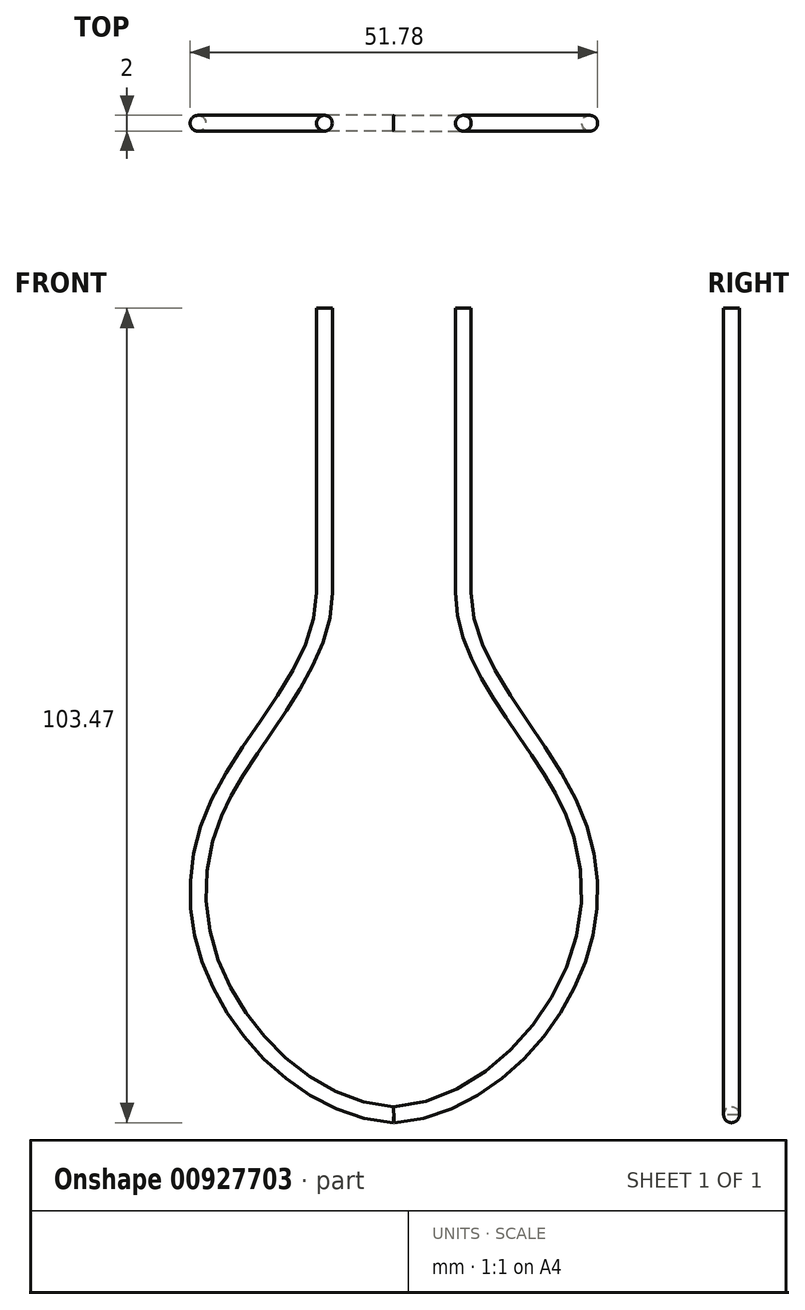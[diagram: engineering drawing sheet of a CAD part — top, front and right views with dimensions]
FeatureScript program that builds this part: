
annotation { "Feature Type Name" : "Feature", "Feature Type Description" : "" }
export const myFeature = defineFeature(function(context is Context, id is Id, definition is map)
    precondition{}
    {
        {
            var Q0;
            Q0=qCreatedBy(makeId("Top.planeOp"),FACE);
            cPlane(context, id + "F0", {"entities" : qUnion([Q0]), "cplaneType" : CPlaneType.OFFSET, "offset" : 83.57 * mm, "width" : 152.4 * mm, "height" : 152.4 * mm});
        }
        {
            var Q0;
            Q0=qCreatedBy(makeId("Front.planeOp"),FACE);
            var sketch = newSketch(context, id + "F1", { "sketchPlane" : qUnion([Q0])});
            skLineSegment(sketch, "E0", {"start": v(8.85, 83.91) * mm, "end": v(8.85, 47.77) * mm});
            skFitSpline(sketch, "E1", {"points": [v(8.85, 47.77) * mm, v(22.55, 20.49) * mm, v(21.46, -3.2) * mm, v(0, -18.58) * mm], "startDerivative": vector(0, -81.85) * mm, "endDerivative": vector(-82.92, -5.2) * mm});
            skSolve(sketch);
        }
        {
            var Q0;
            Q0=qCreatedBy(id+"F0.planeOp",FACE);
            var sketch = newSketch(context, id + "F2", { "sketchPlane" : qUnion([Q0])});
            skCircle(sketch, "E2", {"center": v(8.83, -0.01) * mm, "radius": 1 * mm});
            skSolve(sketch);
        }
        {
            var Q0;
            Q0=makeQuery(id+"F2.imprint","IMPRINT",FACE,{"disambiguationData":[TD([[makeQuery(id+"F2.imprint","IMPRINT",EDGE,{"derivedFrom":sQuery(id+"F2.wireOp",EDGE,"E2")}),1.0]])]});
            var Q1;
            Q1=sQuery(id+"F1.wireOp",EDGE,"E0");
            var Q2;
            Q2=sQuery(id+"F1.wireOp",EDGE,"E1");
            sweep(context, id + "F3", {"profiles" : qUnion([Q0]), "path" : qUnion([Q1, Q2])});
        }
        {
            var Q0;
            Q0=makeQuery(id+"F3.opSweep","SWEPT_BODY",BODY,{"disambiguationData":[OSD([sQuery(id+"F1.wireOp",EDGE,"E1"),sQuery(id+"F2.wireOp",EDGE,"E2")])]});
            var Q1;
            Q1=qCreatedBy(makeId("Right.planeOp"),FACE);
            mirror(context, id + "F4", {"operationType" : NewBodyOperationType.ADD, "entities" : qUnion([Q0]), "mirrorPlane" : qUnion([Q1])});
        }
    });
